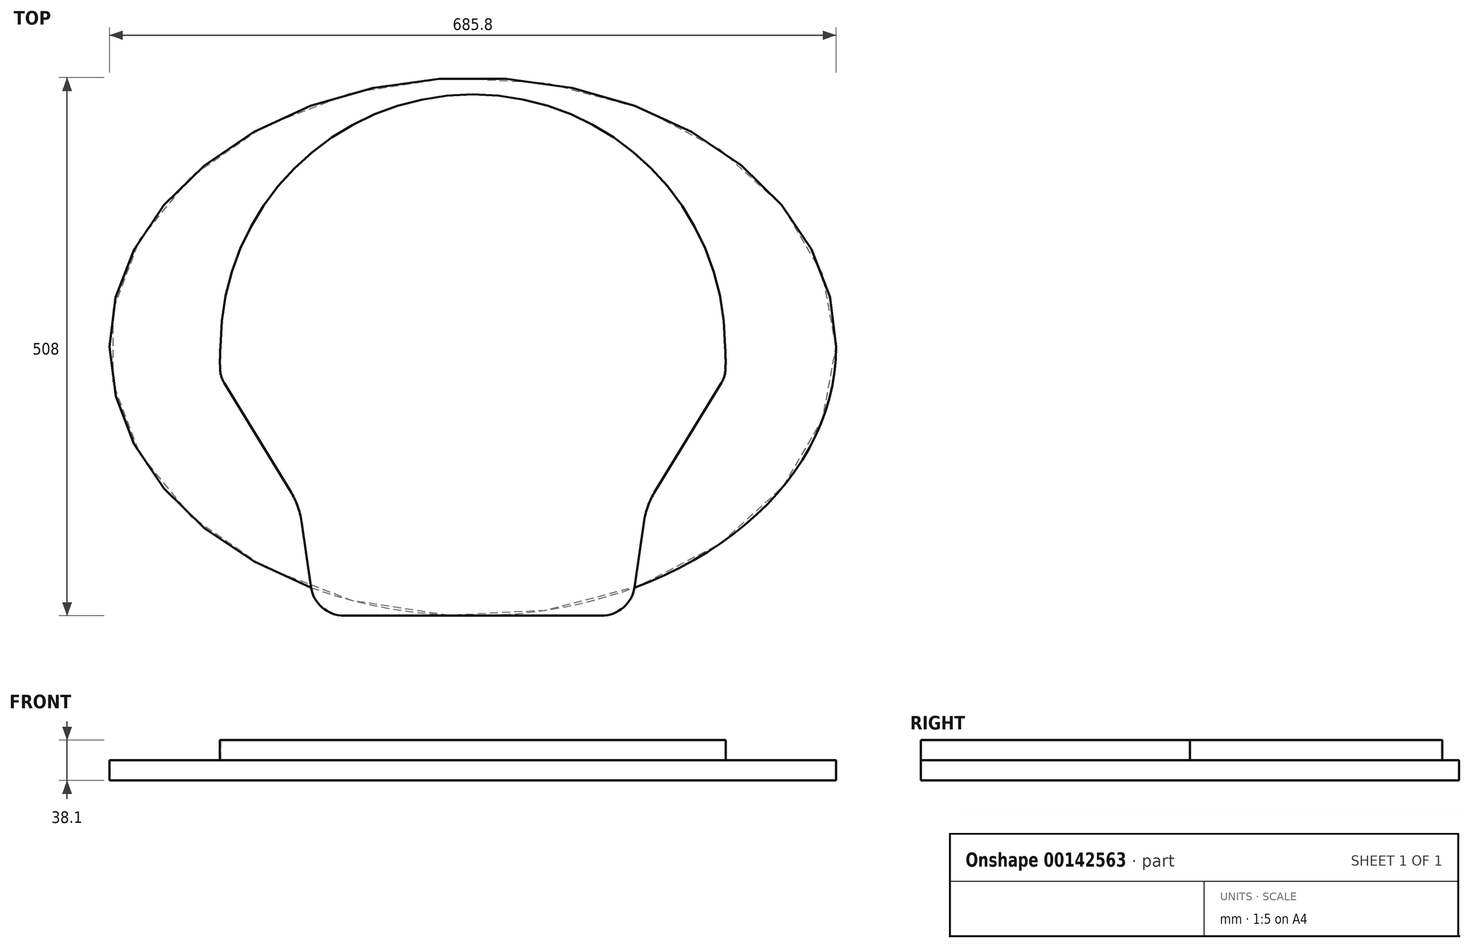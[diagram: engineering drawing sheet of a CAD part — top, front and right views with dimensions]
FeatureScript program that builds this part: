
annotation { "Feature Type Name" : "Feature", "Feature Type Description" : "" }
export const myFeature = defineFeature(function(context is Context, id is Id, definition is map)
    precondition{}
    {
        {
            var Q0;
            Q0=qCreatedBy(makeId("Top.planeOp"),FACE);
            var sketch = newSketch(context, id + "F0", { "sketchPlane" : qUnion([Q0])});
            skEllipse(sketch, "E0", {"center": v(0, 0) * mm, "majorRadius": 342.9 * mm, "minorRadius": 254 * mm, "majorAxis": v(1, 0)});
            skSolve(sketch);
        }
        {
            var Q0;
            Q0=makeQuery(id+"F0.imprint","IMPRINT",FACE,{"disambiguationData":[TD([[makeQuery(id+"F0.imprint","IMPRINT",EDGE,{"derivedFrom":sQuery(id+"F0.wireOp",EDGE,"E0")}),1.0]])]});
            extrude(context, id + "F1", {"entities" : qUnion([Q0]), "depth" : 19.05 * mm});
        }
        {
            var Q0;
            Q0=makeQuery(id+"F1.opExtrude","CAP_FACE",FACE,{"disambiguationData":[OSD([sQuery(id+"F0.wireOp",EDGE,"E0")])],"isStart":false});
            var sketch = newSketch(context, id + "F2", { "sketchPlane" : qUnion([Q0])});
            skLineSegment(sketch, "E1", {"start": v(-238.13, 0) * mm, "end": v(238.12, 0) * mm, "construction": true});
            skPoint(sketch, "E1.endSnap0", {"position": v(-342.9, 0) * mm});
            skLineSegment(sketch, "E2", {"start": v(0, 283.44) * mm, "end": v(0, -254) * mm, "construction": true});
            skPoint(sketch, "E3.startSnap0", {"position": v(0, -254) * mm});
            skLineSegment(sketch, "E4.0", {"start": v(-163.83, -149.86) * mm, "end": v(163.83, -149.86) * mm, "construction": true});
            skLineSegment(sketch, "E5.0", {"start": v(-476.87, -28.58) * mm, "end": v(512.2, -28.57) * mm, "construction": true});
            skArc(sketch, "E6", {"start": v(238.13, 0) * mm, "mid": v(0, 238.13) * mm, "end": v(-238.13, 0) * mm});
            skLineSegment(sketch, "E7.0", {"start": v(148.84, 283.44) * mm, "end": v(148.84, -254) * mm, "construction": true});
            skLineSegment(sketch, "E8.MirrorCS", {"start": v(-148.84, -28.58) * mm, "end": v(-148.84, -254) * mm, "construction": true});
            skLineSegment(sketch, "E9.0", {"start": v(163.83, 0) * mm, "end": v(163.83, -28.57) * mm, "construction": true});
            skLineSegment(sketch, "E10.MirrorCS", {"start": v(-163.83, -28.58) * mm, "end": v(-163.83, -149.86) * mm, "construction": true});
            skLineSegment(sketch, "E11", {"start": v(-161.6, -165.41) * mm, "end": v(-152.76, -226.77) * mm});
            skLineSegment(sketch, "E12", {"start": v(-121.34, -254) * mm, "end": v(121.34, -254) * mm});
            skLineSegment(sketch, "E13", {"start": v(152.76, -226.77) * mm, "end": v(161.6, -165.41) * mm});
            skPoint(sketch, "E14.orphan", {"position": v(-163.83, -332.28) * mm});
            skPoint(sketch, "E15.orphan", {"position": v(-148.84, -332.28) * mm});
            skPoint(sketch, "E16.orphan", {"position": v(148.84, -332.28) * mm});
            skPoint(sketch, "E17.orphan", {"position": v(163.83, -332.28) * mm});
            skPoint(sketch, "E18.orphan", {"position": v(-476.87, -254) * mm});
            skPoint(sketch, "E19.orphan", {"position": v(492.84, 0) * mm});
            skPoint(sketch, "E20.orphan", {"position": v(-472.05, 0) * mm});
            skPoint(sketch, "E21.orphan", {"position": v(163.83, 283.44) * mm});
            skPoint(sketch, "E22.orphan", {"position": v(-163.83, 283.44) * mm});
            skPoint(sketch, "E23.orphan", {"position": v(-148.84, 283.44) * mm});
            skLineSegment(sketch, "E24", {"start": v(-238.13, 0) * mm, "end": v(-238.13, -283.98) * mm, "construction": true});
            skLineSegment(sketch, "E25.MirrorCS", {"start": v(238.13, 0) * mm, "end": v(238.13, -283.98) * mm, "construction": true});
            skLineSegment(sketch, "E26", {"start": v(-172.04, -136.46) * mm, "end": v(-234.76, -34.07) * mm});
            skLineSegment(sketch, "E27.MirrorCS", {"start": v(172.04, -136.46) * mm, "end": v(234.76, -34.07) * mm});
            skLineSegment(sketch, "E28", {"start": v(0, 0) * mm, "end": v(0, -28.57) * mm, "construction": true});
            skLineSegment(sketch, "E29.0", {"start": v(-29.21, 0) * mm, "end": v(-29.2, -28.57) * mm, "construction": true});
            skLineSegment(sketch, "E30.MirrorCS", {"start": v(29.21, 0) * mm, "end": v(29.2, -28.57) * mm, "construction": true});
            skArc(sketch, "E31", {"start": v(-238.48, -21.7) * mm, "mid": v(-238.58, -10.85) * mm, "end": v(-238.13, 0) * mm});
            skArc(sketch, "E32.MirrorCS", {"start": v(238.48, -21.7) * mm, "mid": v(238.58, -10.85) * mm, "end": v(238.13, 0) * mm});
            skPoint(sketch, "E33.visualSharp", {"position": v(-238.13, -28.58) * mm});
            skArc(sketch, "E33.filletArc", {"start": v(-238.48, -21.7) * mm, "mid": v(-237.42, -28.13) * mm, "end": v(-234.76, -34.07) * mm});
            skPoint(sketch, "E34.visualSharp", {"position": v(238.13, -28.58) * mm});
            skArc(sketch, "E34.filletArc", {"start": v(234.76, -34.07) * mm, "mid": v(237.42, -28.13) * mm, "end": v(238.48, -21.7) * mm});
            skPoint(sketch, "E35.visualSharp", {"position": v(163.83, -149.86) * mm});
            skArc(sketch, "E35.filletArc", {"start": v(172.04, -136.46) * mm, "mid": v(165.34, -150.4) * mm, "end": v(161.6, -165.41) * mm});
            skPoint(sketch, "E36.visualSharp", {"position": v(-163.83, -149.86) * mm});
            skArc(sketch, "E36.filletArc", {"start": v(-161.6, -165.41) * mm, "mid": v(-165.34, -150.4) * mm, "end": v(-172.04, -136.46) * mm});
            skPoint(sketch, "E37.visualSharp", {"position": v(-148.84, -254) * mm});
            skArc(sketch, "E37.filletArc", {"start": v(-152.76, -226.77) * mm, "mid": v(-142.13, -246.25) * mm, "end": v(-121.34, -254) * mm});
            skPoint(sketch, "E38.visualSharp", {"position": v(148.84, -254) * mm});
            skArc(sketch, "E38.filletArc", {"start": v(121.34, -254) * mm, "mid": v(142.13, -246.25) * mm, "end": v(152.76, -226.77) * mm});
            skSolve(sketch);
        }
        {
            var Q0;
            Q0 = qSketchRegion(id + "F2", true);
            extrude(context, id + "F3", {"entities" : qUnion([Q0]), "depth" : 19.05 * mm});
        }
    });
